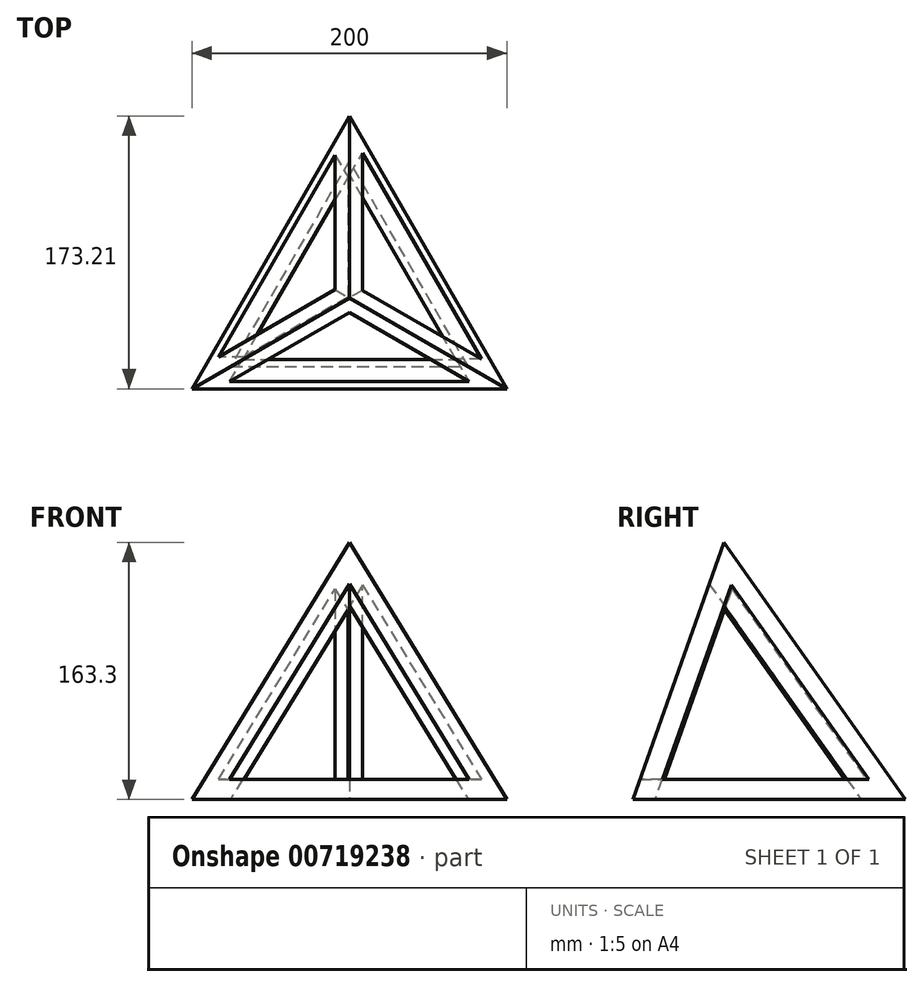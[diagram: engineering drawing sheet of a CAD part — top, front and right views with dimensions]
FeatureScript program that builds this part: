
annotation { "Feature Type Name" : "Feature", "Feature Type Description" : "" }
export const myFeature = defineFeature(function(context is Context, id is Id, definition is map)
    precondition{}
    {
        {
            var Q0;
            Q0=qCreatedBy(makeId("Top.planeOp"),FACE);
            var sketch = newSketch(context, id + "F0", { "sketchPlane" : qUnion([Q0])});
            skLineSegment(sketch, "E0", {"start": v(0, 115.47) * mm, "end": v(100, -57.74) * mm});
            skLineSegment(sketch, "E1", {"start": v(100, -57.74) * mm, "end": v(-100, -57.74) * mm});
            skLineSegment(sketch, "E2", {"start": v(-100, -57.74) * mm, "end": v(0, 115.47) * mm});
            skLineSegment(sketch, "E3", {"start": v(0, 115.47) * mm, "end": v(0, 0) * mm});
            skLineSegment(sketch, "E4", {"start": v(-100, -57.74) * mm, "end": v(0, 0) * mm});
            skLineSegment(sketch, "E5", {"start": v(0, 0) * mm, "end": v(100, -57.74) * mm});
            skPoint(sketch, "E6.orphan", {"position": v(0, -57.74) * mm});
            skLineSegment(sketch, "E7", {"start": v(0, 115.47) * mm, "end": v(0, -57.74) * mm, "construction": true});
            skSolve(sketch);
        }
        {
            assignVariable(context, id + "F1", {"name" : "Angle", "anyValue" : 70.53});
        }
        {
            var Q0;
            Q0=qSketchRegion(id+"F0",true);
            extrude(context, id + "F2", {"entities" : qUnion([Q0]), "depth" : 1000 * mm, "hasDraft" : true, "draftAngle" : (90 - getVariable(context, 'Angle')) * degree, "draftPullDirection" : true});
        }
        {
            var Q0;
            Q0=makeQuery(id+"F2.opExtrude","SWEPT_BODY",BODY,{"disambiguationData":[OSD([sQuery(id+"F0.wireOp",EDGE,"E0"),sQuery(id+"F0.wireOp",EDGE,"E1"),sQuery(id+"F0.wireOp",EDGE,"E2")])]});
            var Q1;
            {var subQ0=sQuery(id+"F0.wireOp",EDGE,"E2");var subQ1=sQuery(id+"F0.wireOp",EDGE,"E1");var subQ2=sQuery(id+"F0.wireOp",EDGE,"E0");Q1=makeQuery(id+"F2.*.draft.opDraft","MERGE",VERTEX,{"derivedFrom":[makeQuery(id+"F2.opExtrude","CAP_VERTEX",VERTEX,{"disambiguationData":[OSD([subQ2,subQ0,sQuery(id+"F0.wireOp",EDGE,"E3")])],"isStart":false}),makeQuery(id+"F2.opExtrude","CAP_VERTEX",VERTEX,{"disambiguationData":[OSD([subQ2,subQ1,sQuery(id+"F0.wireOp",EDGE,"E5")])],"isStart":false}),makeQuery(id+"F2.opExtrude","CAP_VERTEX",VERTEX,{"disambiguationData":[OSD([subQ1,subQ0,sQuery(id+"F0.wireOp",EDGE,"E4")])],"isStart":false})]});}
            transform(context, id + "F3", {"entities" : qUnion([Q0]), "transformType" : TransformType.SCALE_UNIFORMLY, "scale" : 0.8, "scalePoint" : qUnion([Q1]), "makeCopy" : true});
        }
        {
            var Q0;
            Q0=makeQuery(id+"F3.opPattern","COPY",BODY,{"derivedFrom":makeQuery(id+"F2.opExtrude","SWEPT_BODY",BODY,{"disambiguationData":[OSD([sQuery(id+"F0.wireOp",EDGE,"E0"),sQuery(id+"F0.wireOp",EDGE,"E1"),sQuery(id+"F0.wireOp",EDGE,"E2")])]}),"instanceName":"1"});
            transform(context, id + "F4", {"entities" : qUnion([Q0]), "transformType" : TransformType.TRANSLATION_3D, "dx" : 0 * mm, "dy" : 0 * mm, "dz" : -20 * mm, "makeCopy" : false});
        }
        {
            var Q0;
            Q0=makeQuery(id+"F3.opPattern","COPY",BODY,{"derivedFrom":makeQuery(id+"F2.opExtrude","SWEPT_BODY",BODY,{"disambiguationData":[OSD([sQuery(id+"F0.wireOp",EDGE,"E0"),sQuery(id+"F0.wireOp",EDGE,"E1"),sQuery(id+"F0.wireOp",EDGE,"E2")])]}),"instanceName":"1"});
            transform(context, id + "F5", {"entities" : qUnion([Q0]), "transformType" : TransformType.TRANSLATION_3D, "dx" : 0 * mm, "dy" : 0 * mm, "dz" : 0 * mm, "makeCopy" : true});
        }
        {
            var Q0;
            Q0=qCreatedBy(makeId("Top.planeOp"),FACE);
            var sketch = newSketch(context, id + "F6", { "sketchPlane" : qUnion([Q0])});
            skLineSegment(sketch, "E8", {"start": v(0, 0) * mm, "end": v(-12.7, -7.33) * mm});
            skLineSegment(sketch, "E9", {"start": v(0, 0) * mm, "end": v(-27.29, 0) * mm, "construction": true});
            skLineSegment(sketch, "E10", {"start": v(0, 0) * mm, "end": v(0, -13.85) * mm});
            skLineSegment(sketch, "E11", {"start": v(0, 0) * mm, "end": v(-15.07, 8.7) * mm});
            skSolve(sketch);
        }
        {
            var Q0;
            Q0=makeQuery(id+"F5.opPattern","COPY",BODY,{"derivedFrom":makeQuery(id+"F3.opPattern","COPY",BODY,{"derivedFrom":makeQuery(id+"F2.opExtrude","SWEPT_BODY",BODY,{"disambiguationData":[OSD([sQuery(id+"F0.wireOp",EDGE,"E0"),sQuery(id+"F0.wireOp",EDGE,"E1"),sQuery(id+"F0.wireOp",EDGE,"E2")])]}),"instanceName":"1"}),"instanceName":"1"});
            var Q1;
            Q1=sQuery(id+"F6.wireOp",EDGE,"E8");
            transform(context, id + "F7", {"entities" : qUnion([Q0]), "transformType" : TransformType.TRANSLATION_ENTITY, "oppositeDirectionEntity" : true, "transformLine" : qUnion([Q1]), "makeCopy" : true});
        }
        {
            var Q0;
            Q0=makeQuery(id+"F7.opPattern","COPY",BODY,{"derivedFrom":makeQuery(id+"F5.opPattern","COPY",BODY,{"derivedFrom":makeQuery(id+"F3.opPattern","COPY",BODY,{"derivedFrom":makeQuery(id+"F2.opExtrude","SWEPT_BODY",BODY,{"disambiguationData":[OSD([sQuery(id+"F0.wireOp",EDGE,"E0"),sQuery(id+"F0.wireOp",EDGE,"E1"),sQuery(id+"F0.wireOp",EDGE,"E2")])]}),"instanceName":"1"}),"instanceName":"1"}),"instanceName":"1"});
            var Q1;
            Q1=makeQuery(id+"F2.opExtrude","SWEPT_BODY",BODY,{"disambiguationData":[OSD([sQuery(id+"F0.wireOp",EDGE,"E0"),sQuery(id+"F0.wireOp",EDGE,"E1"),sQuery(id+"F0.wireOp",EDGE,"E2")])]});
            booleanBodies(context, id + "F8", {"operationType" : BooleanOperationType.SUBTRACTION, "tools" : qUnion([Q0]), "targets" : qUnion([Q1]), "keepTools" : true});
        }
        {
            var Q0;
            Q0=makeQuery(id+"F7.opPattern","COPY",BODY,{"derivedFrom":makeQuery(id+"F5.opPattern","COPY",BODY,{"derivedFrom":makeQuery(id+"F3.opPattern","COPY",BODY,{"derivedFrom":makeQuery(id+"F2.opExtrude","SWEPT_BODY",BODY,{"disambiguationData":[OSD([sQuery(id+"F0.wireOp",EDGE,"E0"),sQuery(id+"F0.wireOp",EDGE,"E1"),sQuery(id+"F0.wireOp",EDGE,"E2")])]}),"instanceName":"1"}),"instanceName":"1"}),"instanceName":"1"});
            deleteBodies(context, id + "F9", {"entities" : qUnion([Q0])});
        }
        {
            var Q0;
            Q0=makeQuery(id+"F3.opPattern","COPY",BODY,{"derivedFrom":makeQuery(id+"F2.opExtrude","SWEPT_BODY",BODY,{"disambiguationData":[OSD([sQuery(id+"F0.wireOp",EDGE,"E0"),sQuery(id+"F0.wireOp",EDGE,"E1"),sQuery(id+"F0.wireOp",EDGE,"E2")])]}),"instanceName":"1"});
            var Q1;
            Q1=sQuery(id+"F6.wireOp",EDGE,"E11");
            transform(context, id + "F10", {"entities" : qUnion([Q0]), "transformType" : TransformType.TRANSLATION_ENTITY, "oppositeDirectionEntity" : false, "transformLine" : qUnion([Q1]), "makeCopy" : true});
        }
        {
            var Q0;
            Q0=makeQuery(id+"F10.opPattern","COPY",BODY,{"derivedFrom":makeQuery(id+"F3.opPattern","COPY",BODY,{"derivedFrom":makeQuery(id+"F2.opExtrude","SWEPT_BODY",BODY,{"disambiguationData":[OSD([sQuery(id+"F0.wireOp",EDGE,"E0"),sQuery(id+"F0.wireOp",EDGE,"E1"),sQuery(id+"F0.wireOp",EDGE,"E2")])]}),"instanceName":"1"}),"instanceName":"1"});
            var Q1;
            Q1=makeQuery(id+"F2.opExtrude","SWEPT_BODY",BODY,{"disambiguationData":[OSD([sQuery(id+"F0.wireOp",EDGE,"E0"),sQuery(id+"F0.wireOp",EDGE,"E1"),sQuery(id+"F0.wireOp",EDGE,"E2")])]});
            booleanBodies(context, id + "F11", {"operationType" : BooleanOperationType.SUBTRACTION, "tools" : qUnion([Q0]), "targets" : qUnion([Q1])});
        }
        {
            var Q0;
            Q0=makeQuery(id+"F5.opPattern","COPY",BODY,{"derivedFrom":makeQuery(id+"F3.opPattern","COPY",BODY,{"derivedFrom":makeQuery(id+"F2.opExtrude","SWEPT_BODY",BODY,{"disambiguationData":[OSD([sQuery(id+"F0.wireOp",EDGE,"E0"),sQuery(id+"F0.wireOp",EDGE,"E1"),sQuery(id+"F0.wireOp",EDGE,"E2")])]}),"instanceName":"1"}),"instanceName":"1"});
            deleteBodies(context, id + "F12", {"entities" : qUnion([Q0])});
        }
        {
            var Q0;
            Q0=makeQuery(id+"F3.opPattern","COPY",BODY,{"derivedFrom":makeQuery(id+"F2.opExtrude","SWEPT_BODY",BODY,{"disambiguationData":[OSD([sQuery(id+"F0.wireOp",EDGE,"E0"),sQuery(id+"F0.wireOp",EDGE,"E1"),sQuery(id+"F0.wireOp",EDGE,"E2")])]}),"instanceName":"1"});
            var Q1;
            Q1=sQuery(id+"F6.wireOp",EDGE,"E10");
            transform(context, id + "F13", {"entities" : qUnion([Q0]), "transformType" : TransformType.TRANSLATION_ENTITY, "oppositeDirectionEntity" : false, "transformLine" : qUnion([Q1]), "makeCopy" : true});
        }
        {
            var Q0;
            Q0=makeQuery(id+"F13.opPattern","COPY",BODY,{"derivedFrom":makeQuery(id+"F3.opPattern","COPY",BODY,{"derivedFrom":makeQuery(id+"F2.opExtrude","SWEPT_BODY",BODY,{"disambiguationData":[OSD([sQuery(id+"F0.wireOp",EDGE,"E0"),sQuery(id+"F0.wireOp",EDGE,"E1"),sQuery(id+"F0.wireOp",EDGE,"E2")])]}),"instanceName":"1"}),"instanceName":"1"});
            var Q1;
            Q1=makeQuery(id+"F2.opExtrude","SWEPT_BODY",BODY,{"disambiguationData":[OSD([sQuery(id+"F0.wireOp",EDGE,"E0"),sQuery(id+"F0.wireOp",EDGE,"E1"),sQuery(id+"F0.wireOp",EDGE,"E2")])]});
            booleanBodies(context, id + "F14", {"operationType" : BooleanOperationType.SUBTRACTION, "tools" : qUnion([Q0]), "targets" : qUnion([Q1])});
        }
        {
            var Q0;
            Q0=makeQuery(id+"F3.opPattern","COPY",BODY,{"derivedFrom":makeQuery(id+"F2.opExtrude","SWEPT_BODY",BODY,{"disambiguationData":[OSD([sQuery(id+"F0.wireOp",EDGE,"E0"),sQuery(id+"F0.wireOp",EDGE,"E1"),sQuery(id+"F0.wireOp",EDGE,"E2")])]}),"instanceName":"1"});
            transform(context, id + "F15", {"entities" : qUnion([Q0]), "transformType" : TransformType.TRANSLATION_3D, "dx" : 0 * mm, "dy" : 0 * mm, "dz" : -20 * mm, "makeCopy" : false});
        }
        {
            var Q0;
            Q0=makeQuery(id+"F3.opPattern","COPY",BODY,{"derivedFrom":makeQuery(id+"F2.opExtrude","SWEPT_BODY",BODY,{"disambiguationData":[OSD([sQuery(id+"F0.wireOp",EDGE,"E0"),sQuery(id+"F0.wireOp",EDGE,"E1"),sQuery(id+"F0.wireOp",EDGE,"E2")])]}),"instanceName":"1"});
            var Q1;
            Q1=makeQuery(id+"F2.opExtrude","SWEPT_BODY",BODY,{"disambiguationData":[OSD([sQuery(id+"F0.wireOp",EDGE,"E0"),sQuery(id+"F0.wireOp",EDGE,"E1"),sQuery(id+"F0.wireOp",EDGE,"E2")])]});
            booleanBodies(context, id + "F16", {"operationType" : BooleanOperationType.SUBTRACTION, "tools" : qUnion([Q0]), "targets" : qUnion([Q1])});
        }
    });
